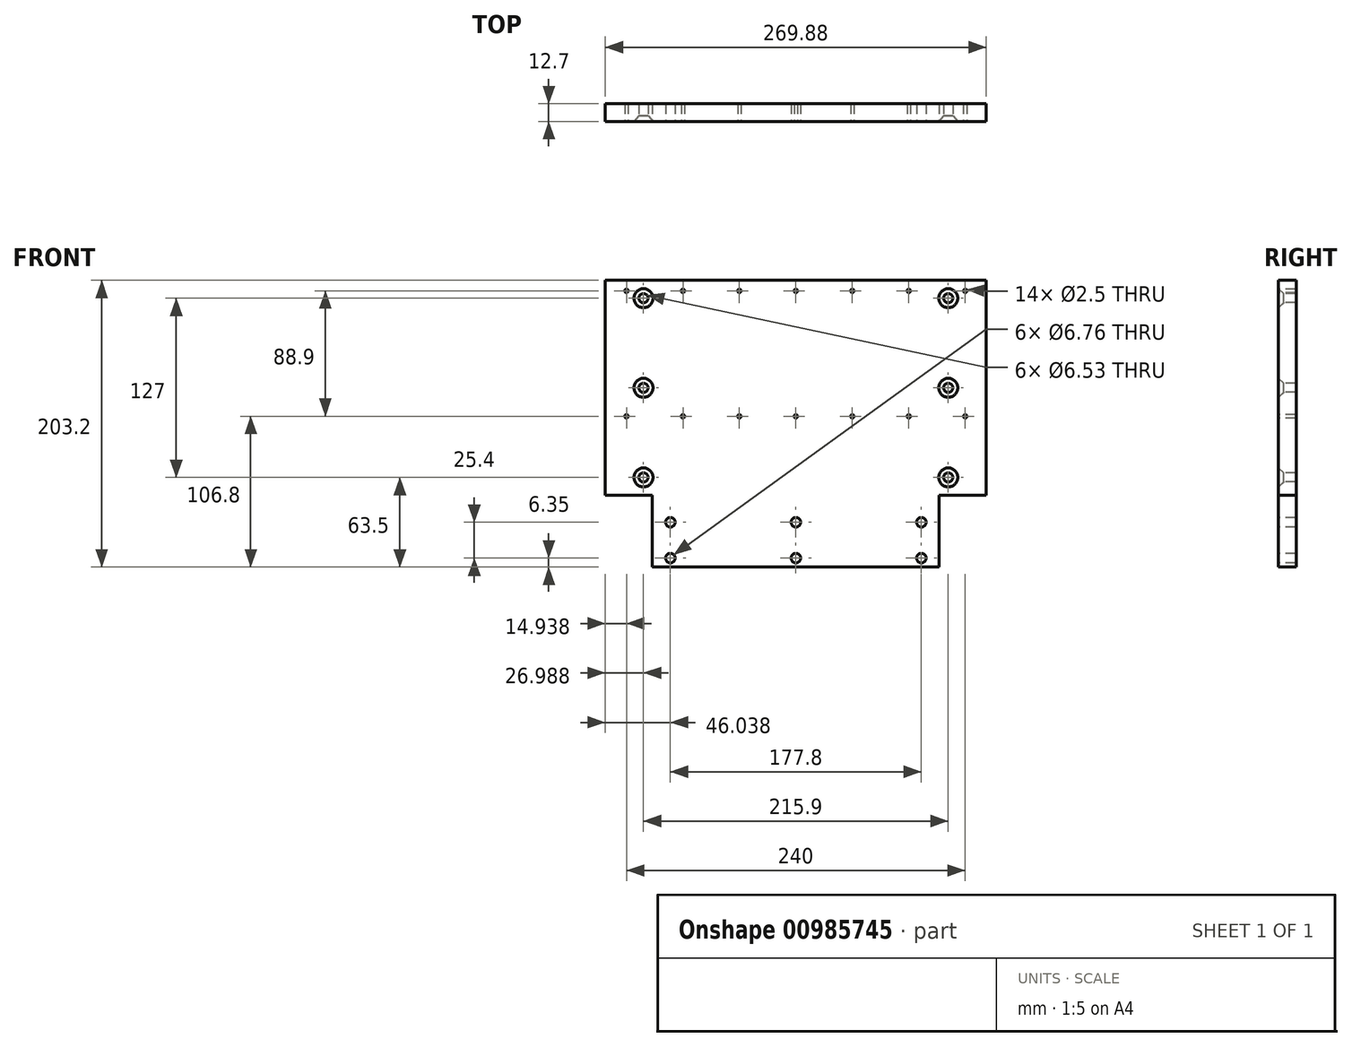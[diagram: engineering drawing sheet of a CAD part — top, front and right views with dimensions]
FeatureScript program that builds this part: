
annotation { "Feature Type Name" : "Feature", "Feature Type Description" : "" }
export const myFeature = defineFeature(function(context is Context, id is Id, definition is map)
    precondition{}
    {
        {
            var Q0;
            Q0=qCreatedBy(makeId("Front.planeOp"),FACE);
            var sketch = newSketch(context, id + "F0", { "sketchPlane" : qUnion([Q0])});
            skLineSegment(sketch, "E0.bottom", {"start": v(0, 0) * mm, "end": v(269.88, 0) * mm});
            skLineSegment(sketch, "E0.top", {"start": v(0, 203.2) * mm, "end": v(269.88, 203.2) * mm});
            skLineSegment(sketch, "E0.left", {"start": v(0, 0) * mm, "end": v(0, 203.2) * mm});
            skLineSegment(sketch, "E0.right", {"start": v(269.88, 0) * mm, "end": v(269.88, 203.2) * mm});
            skSolve(sketch);
        }
        {
            var Q0;
            Q0 = qSketchRegion(id + "F0", true);
            extrude(context, id + "F1", {"entities" : qUnion([Q0]), "depth" : 12.7 * mm, "offsetDistance" : 25.4 * mm});
        }
        {
            var Q0;
            Q0=makeQuery(id+"F1.opExtrude","CAP_FACE",FACE,{"disambiguationData":[OSD([sQuery(id+"F0.wireOp",EDGE,"E0.bottom"),sQuery(id+"F0.wireOp",EDGE,"E0.top"),sQuery(id+"F0.wireOp",EDGE,"E0.left"),sQuery(id+"F0.wireOp",EDGE,"E0.right")])],"isStart":false});
            var sketch = newSketch(context, id + "F2", { "sketchPlane" : qUnion([Q0])});
            skLineSegment(sketch, "E1.bottom", {"start": v(0, 50.8) * mm, "end": v(33.34, 50.8) * mm});
            skLineSegment(sketch, "E1.top", {"start": v(0, 0) * mm, "end": v(33.34, 0) * mm});
            skLineSegment(sketch, "E1.left", {"start": v(0, 50.8) * mm, "end": v(0, 0) * mm});
            skLineSegment(sketch, "E1.right", {"start": v(33.34, 50.8) * mm, "end": v(33.34, 0) * mm});
            skLineSegment(sketch, "E2.bottom", {"start": v(236.54, 0) * mm, "end": v(269.88, 0) * mm});
            skLineSegment(sketch, "E2.top", {"start": v(236.54, 50.8) * mm, "end": v(269.88, 50.8) * mm});
            skLineSegment(sketch, "E2.left", {"start": v(236.54, 0) * mm, "end": v(236.54, 50.8) * mm});
            skLineSegment(sketch, "E2.right", {"start": v(269.88, 0) * mm, "end": v(269.88, 50.8) * mm});
            skLineSegment(sketch, "E3", {"start": v(236.54, 50.8) * mm, "end": v(33.34, 50.8) * mm, "construction": true});
            skLineSegment(sketch, "E4", {"start": v(134.94, 50.8) * mm, "end": v(134.94, 0) * mm, "construction": true});
            skSolve(sketch);
        }
        {
            var Q0;
            Q0 = qSketchRegion(id + "F2", true);
            extrude(context, id + "F3", {"entities" : qUnion([Q0]), "operationType" : NewBodyOperationType.REMOVE, "endBound" : BoundingType.UP_TO_NEXT, "oppositeDirection" : true, "depth" : 25.4 * mm, "offsetDistance" : 25.4 * mm});
        }
        {
            var Q0;
            Q0=makeQuery(id+"F1.opExtrude","CAP_FACE",FACE,{"disambiguationData":[OSD([sQuery(id+"F0.wireOp",EDGE,"E0.bottom"),sQuery(id+"F0.wireOp",EDGE,"E0.top"),sQuery(id+"F0.wireOp",EDGE,"E0.left"),sQuery(id+"F0.wireOp",EDGE,"E0.right")])],"isStart":false});
            var sketch = newSketch(context, id + "F4", { "sketchPlane" : qUnion([Q0])});
            skLineSegment(sketch, "E5", {"start": v(46.04, 6.35) * mm, "end": v(46.04, 31.75) * mm, "construction": true});
            skLineSegment(sketch, "E6", {"start": v(46.04, 31.75) * mm, "end": v(223.84, 31.75) * mm, "construction": true});
            skLineSegment(sketch, "E7", {"start": v(223.84, 31.75) * mm, "end": v(223.84, 6.35) * mm, "construction": true});
            skLineSegment(sketch, "E8", {"start": v(223.84, 6.35) * mm, "end": v(46.04, 6.35) * mm, "construction": true});
            skLineSegment(sketch, "E9", {"start": v(134.94, 0) * mm, "end": v(134.94, 6.35) * mm, "construction": true});
            skPoint(sketch, "E10", {"position": v(46.04, 31.75) * mm});
            skPoint(sketch, "E11", {"position": v(46.04, 6.35) * mm});
            skPoint(sketch, "E12", {"position": v(134.94, 6.35) * mm});
            skPoint(sketch, "E13", {"position": v(134.94, 31.75) * mm});
            skPoint(sketch, "E14", {"position": v(223.84, 31.75) * mm});
            skPoint(sketch, "E15", {"position": v(223.84, 6.35) * mm});
            skSolve(sketch);
        }
        {
            var Q0;
            Q0=sQuery(id+"F4.wireOp",VERTEX,"550244c6-e1ca-4aef-825c-094afa19737b");
            var Q1;
            Q1=sQuery(id+"F4.wireOp",VERTEX,"16170d57-3aca-429f-873f-952340130de8");
            var Q2;
            Q2=sQuery(id+"F4.wireOp",VERTEX,"46ebe26b-f67d-4894-8c40-8e21d605be01");
            var Q3;
            Q3=sQuery(id+"F4.wireOp",VERTEX,"38b6fee7-94b1-4896-bb24-06663a68188f");
            var Q4;
            Q4=sQuery(id+"F4.wireOp",VERTEX,"E14");
            var Q5;
            Q5=sQuery(id+"F4.wireOp",VERTEX,"E15");
            var Q6;
            Q6=sQuery(id+"F4.wireOp",VERTEX,"E12");
            var Q7;
            Q7=sQuery(id+"F4.wireOp",VERTEX,"E13");
            var Q8;
            Q8=sQuery(id+"F4.wireOp",VERTEX,"E10");
            var Q9;
            Q9=sQuery(id+"F4.wireOp",VERTEX,"E11");
            var Q10;
            Q10=sQuery(id+"F4.wireOp",VERTEX,"3891a193-d809-4e0f-8c4e-d58b839b577c");
            var Q11;
            Q11=sQuery(id+"F4.wireOp",VERTEX,"20979e8a-4ba3-4fcb-ac95-f96472d8bf8d");
            var Q12;
            Q12=makeQuery(id+"F1.opExtrude","SWEPT_BODY",BODY,{"disambiguationData":[OSD([sQuery(id+"F0.wireOp",EDGE,"E0.bottom"),sQuery(id+"F0.wireOp",EDGE,"E0.top"),sQuery(id+"F0.wireOp",EDGE,"E0.left"),sQuery(id+"F0.wireOp",EDGE,"E0.right")])]});
            hole(context, id + "F5", {"style" : HoleStyle.SIMPLE, "endStyle" : HoleEndStyle.THROUGH, "standardTappedOrClearance" : lookupTablePath({ "fit" : "Free", "standard" : "ANSI", "size" : "1/4", "type" : "Clearance" }), "standardBlindInLast" : lookupTablePath({ "fit" : "Free", "standard" : "ANSI", "engagement" : "75%", "pitch" : "20 tpi", "size" : "1/4", "type" : "Clearance & tapped" }), "holeDiameter" : 6.76 * mm, "majorDiameter" : 6.35 * mm, "isTappedThrough" : true, "tappedDepth" : 19.05 * mm, "tapClearance" : 3, "startFromSketch" : true, "locations" : qUnion([Q0, Q1, Q2, Q3, Q4, Q5, Q6, Q7, Q8, Q9, Q10, Q11]), "scope" : qUnion([Q12])});
        }
        {
            var Q0;
            Q0=makeQuery(id+"F1.opExtrude","CAP_FACE",FACE,{"disambiguationData":[OSD([sQuery(id+"F0.wireOp",EDGE,"E0.bottom"),sQuery(id+"F0.wireOp",EDGE,"E0.top"),sQuery(id+"F0.wireOp",EDGE,"E0.left"),sQuery(id+"F0.wireOp",EDGE,"E0.right")])],"isStart":false});
            var sketch = newSketch(context, id + "F6", { "sketchPlane" : qUnion([Q0])});
            skLineSegment(sketch, "E16", {"start": v(54.94, 195.7) * mm, "end": v(94.94, 195.7) * mm, "construction": true});
            skLineSegment(sketch, "E17", {"start": v(94.94, 195.7) * mm, "end": v(134.94, 195.7) * mm, "construction": true});
            skLineSegment(sketch, "E18", {"start": v(134.94, 195.7) * mm, "end": v(174.94, 195.7) * mm, "construction": true});
            skLineSegment(sketch, "E19", {"start": v(174.94, 195.7) * mm, "end": v(214.94, 195.7) * mm, "construction": true});
            skLineSegment(sketch, "E20", {"start": v(214.94, 195.7) * mm, "end": v(214.94, 106.8) * mm, "construction": true});
            skLineSegment(sketch, "E21", {"start": v(214.94, 106.8) * mm, "end": v(174.94, 106.8) * mm, "construction": true});
            skLineSegment(sketch, "E22", {"start": v(174.94, 106.8) * mm, "end": v(134.94, 106.8) * mm, "construction": true});
            skLineSegment(sketch, "E23", {"start": v(134.94, 106.8) * mm, "end": v(94.94, 106.8) * mm, "construction": true});
            skLineSegment(sketch, "E24", {"start": v(94.94, 106.8) * mm, "end": v(54.94, 106.8) * mm, "construction": true});
            skLineSegment(sketch, "E25", {"start": v(54.94, 106.8) * mm, "end": v(54.94, 195.7) * mm, "construction": true});
            skLineSegment(sketch, "E26", {"start": v(94.94, 195.7) * mm, "end": v(94.94, 106.8) * mm, "construction": true});
            skLineSegment(sketch, "E27", {"start": v(134.94, 195.7) * mm, "end": v(134.94, 106.8) * mm, "construction": true});
            skLineSegment(sketch, "E28", {"start": v(174.94, 195.7) * mm, "end": v(174.94, 106.8) * mm, "construction": true});
            skLineSegment(sketch, "E29", {"start": v(134.94, 195.7) * mm, "end": v(134.94, 203.2) * mm, "construction": true});
            skPoint(sketch, "E30", {"position": v(54.94, 195.7) * mm});
            skPoint(sketch, "E31", {"position": v(54.94, 106.8) * mm});
            skPoint(sketch, "E32", {"position": v(94.94, 195.7) * mm});
            skPoint(sketch, "E33", {"position": v(94.94, 106.8) * mm});
            skPoint(sketch, "E34", {"position": v(134.94, 195.7) * mm});
            skPoint(sketch, "E35", {"position": v(134.94, 106.8) * mm});
            skPoint(sketch, "E36", {"position": v(174.94, 195.7) * mm});
            skPoint(sketch, "E37", {"position": v(174.94, 106.8) * mm});
            skPoint(sketch, "E38", {"position": v(214.94, 195.7) * mm});
            skPoint(sketch, "E39", {"position": v(214.94, 106.8) * mm});
            skLineSegment(sketch, "E40", {"start": v(214.94, 195.7) * mm, "end": v(254.94, 195.7) * mm, "construction": true});
            skLineSegment(sketch, "E41", {"start": v(254.94, 195.7) * mm, "end": v(254.94, 106.8) * mm, "construction": true});
            skLineSegment(sketch, "E42", {"start": v(254.94, 106.8) * mm, "end": v(214.94, 106.8) * mm, "construction": true});
            skLineSegment(sketch, "E43", {"start": v(54.94, 195.7) * mm, "end": v(14.94, 195.7) * mm, "construction": true});
            skLineSegment(sketch, "E44", {"start": v(14.94, 195.7) * mm, "end": v(14.94, 106.8) * mm, "construction": true});
            skLineSegment(sketch, "E45", {"start": v(14.94, 106.8) * mm, "end": v(54.94, 106.8) * mm, "construction": true});
            skPoint(sketch, "E46", {"position": v(14.94, 195.7) * mm});
            skPoint(sketch, "E47", {"position": v(14.94, 106.8) * mm});
            skPoint(sketch, "E48", {"position": v(254.94, 195.7) * mm});
            skPoint(sketch, "E49", {"position": v(254.94, 106.8) * mm});
            skSolve(sketch);
        }
        {
            var Q0;
            Q0=sQuery(id+"F6.wireOp",VERTEX,"E30");
            var Q1;
            Q1=sQuery(id+"F6.wireOp",VERTEX,"E32");
            var Q2;
            Q2=sQuery(id+"F6.wireOp",VERTEX,"E34");
            var Q3;
            Q3=sQuery(id+"F6.wireOp",VERTEX,"E36");
            var Q4;
            Q4=sQuery(id+"F6.wireOp",VERTEX,"E38");
            var Q5;
            Q5=sQuery(id+"F6.wireOp",VERTEX,"E39");
            var Q6;
            Q6=sQuery(id+"F6.wireOp",VERTEX,"E37");
            var Q7;
            Q7=sQuery(id+"F6.wireOp",VERTEX,"E35");
            var Q8;
            Q8=sQuery(id+"F6.wireOp",VERTEX,"E33");
            var Q9;
            Q9=sQuery(id+"F6.wireOp",VERTEX,"E31");
            var Q10;
            Q10=sQuery(id+"F6.wireOp",VERTEX,"E46");
            var Q11;
            Q11=sQuery(id+"F6.wireOp",VERTEX,"E47");
            var Q12;
            Q12=sQuery(id+"F6.wireOp",VERTEX,"E48");
            var Q13;
            Q13=sQuery(id+"F6.wireOp",VERTEX,"E49");
            var Q14;
            Q14=makeQuery(id+"F1.opExtrude","SWEPT_BODY",BODY,{"disambiguationData":[OSD([sQuery(id+"F0.wireOp",EDGE,"E0.bottom"),sQuery(id+"F0.wireOp",EDGE,"E0.top"),sQuery(id+"F0.wireOp",EDGE,"E0.left"),sQuery(id+"F0.wireOp",EDGE,"E0.right")])]});
            hole(context, id + "F7", {"style" : HoleStyle.SIMPLE, "endStyle" : HoleEndStyle.BLIND, "standardTappedOrClearance" : lookupTablePath({ "standard" : "ISO", "engagement" : "75%", "pitch" : "0.5 mm", "size" : "M3", "type" : "Tapped" }), "standardBlindInLast" : lookupTablePath({ "standard" : "ISO", "fit" : "Normal", "engagement" : "75%", "pitch" : "0.5 mm", "size" : "M3", "type" : "Clearance & tapped" }), "holeDiameter" : 2.5 * mm, "majorDiameter" : 3 * mm, "showTappedDepth" : true, "holeDepth" : 20.55 * mm, "isTappedThrough" : true, "tappedDepth" : 19.05 * mm, "tapClearance" : 3, "startFromSketch" : true, "locations" : qUnion([Q0, Q1, Q2, Q3, Q4, Q5, Q6, Q7, Q8, Q9, Q10, Q11, Q12, Q13]), "scope" : qUnion([Q14])});
        }
        {
            var Q0;
            Q0=makeQuery(id+"F1.opExtrude","CAP_FACE",FACE,{"disambiguationData":[OSD([sQuery(id+"F0.wireOp",EDGE,"E0.bottom"),sQuery(id+"F0.wireOp",EDGE,"E0.top"),sQuery(id+"F0.wireOp",EDGE,"E0.left"),sQuery(id+"F0.wireOp",EDGE,"E0.right")])],"isStart":false});
            var sketch = newSketch(context, id + "F8", { "sketchPlane" : qUnion([Q0])});
            skLineSegment(sketch, "E50", {"start": v(26.99, 190.5) * mm, "end": v(26.99, 63.5) * mm, "construction": true});
            skLineSegment(sketch, "E51", {"start": v(26.99, 63.5) * mm, "end": v(242.89, 63.5) * mm, "construction": true});
            skLineSegment(sketch, "E52", {"start": v(242.89, 63.5) * mm, "end": v(242.89, 190.5) * mm, "construction": true});
            skLineSegment(sketch, "E53", {"start": v(242.89, 190.5) * mm, "end": v(26.99, 190.5) * mm, "construction": true});
            skLineSegment(sketch, "E54", {"start": v(134.94, 0) * mm, "end": v(134.94, 63.5) * mm, "construction": true});
            skPoint(sketch, "E55", {"position": v(26.99, 190.5) * mm});
            skPoint(sketch, "E56", {"position": v(26.99, 63.5) * mm});
            skPoint(sketch, "E57", {"position": v(242.89, 190.5) * mm});
            skPoint(sketch, "E58", {"position": v(242.89, 127) * mm});
            skPoint(sketch, "E59", {"position": v(26.99, 127) * mm});
            skPoint(sketch, "E60", {"position": v(242.89, 63.5) * mm});
            skSolve(sketch);
        }
        {
            var Q0;
            Q0=sQuery(id+"F8.wireOp",VERTEX,"E55");
            var Q1;
            Q1=sQuery(id+"F8.wireOp",VERTEX,"E59");
            var Q2;
            Q2=sQuery(id+"F8.wireOp",VERTEX,"E56");
            var Q3;
            Q3=sQuery(id+"F8.wireOp",VERTEX,"E60");
            var Q4;
            Q4=sQuery(id+"F8.wireOp",VERTEX,"E58");
            var Q5;
            Q5=sQuery(id+"F8.wireOp",VERTEX,"E57");
            var Q6;
            Q6=makeQuery(id+"F1.opExtrude","SWEPT_BODY",BODY,{"disambiguationData":[OSD([sQuery(id+"F0.wireOp",EDGE,"E0.bottom"),sQuery(id+"F0.wireOp",EDGE,"E0.top"),sQuery(id+"F0.wireOp",EDGE,"E0.left"),sQuery(id+"F0.wireOp",EDGE,"E0.right")])]});
            hole(context, id + "F9", {"style" : HoleStyle.C_SINK, "endStyle" : HoleEndStyle.THROUGH, "holeDiameter" : 6.53 * mm, "cSinkDiameter" : 13.5 * mm, "cSinkAngle" : 82 * degree, "majorDiameter" : 6.35 * mm, "isTappedThrough" : true, "tappedDepth" : 19.05 * mm, "tapClearance" : 3, "startFromSketch" : true, "locations" : qUnion([Q0, Q1, Q2, Q3, Q4, Q5]), "scope" : qUnion([Q6])});
        }
    });
